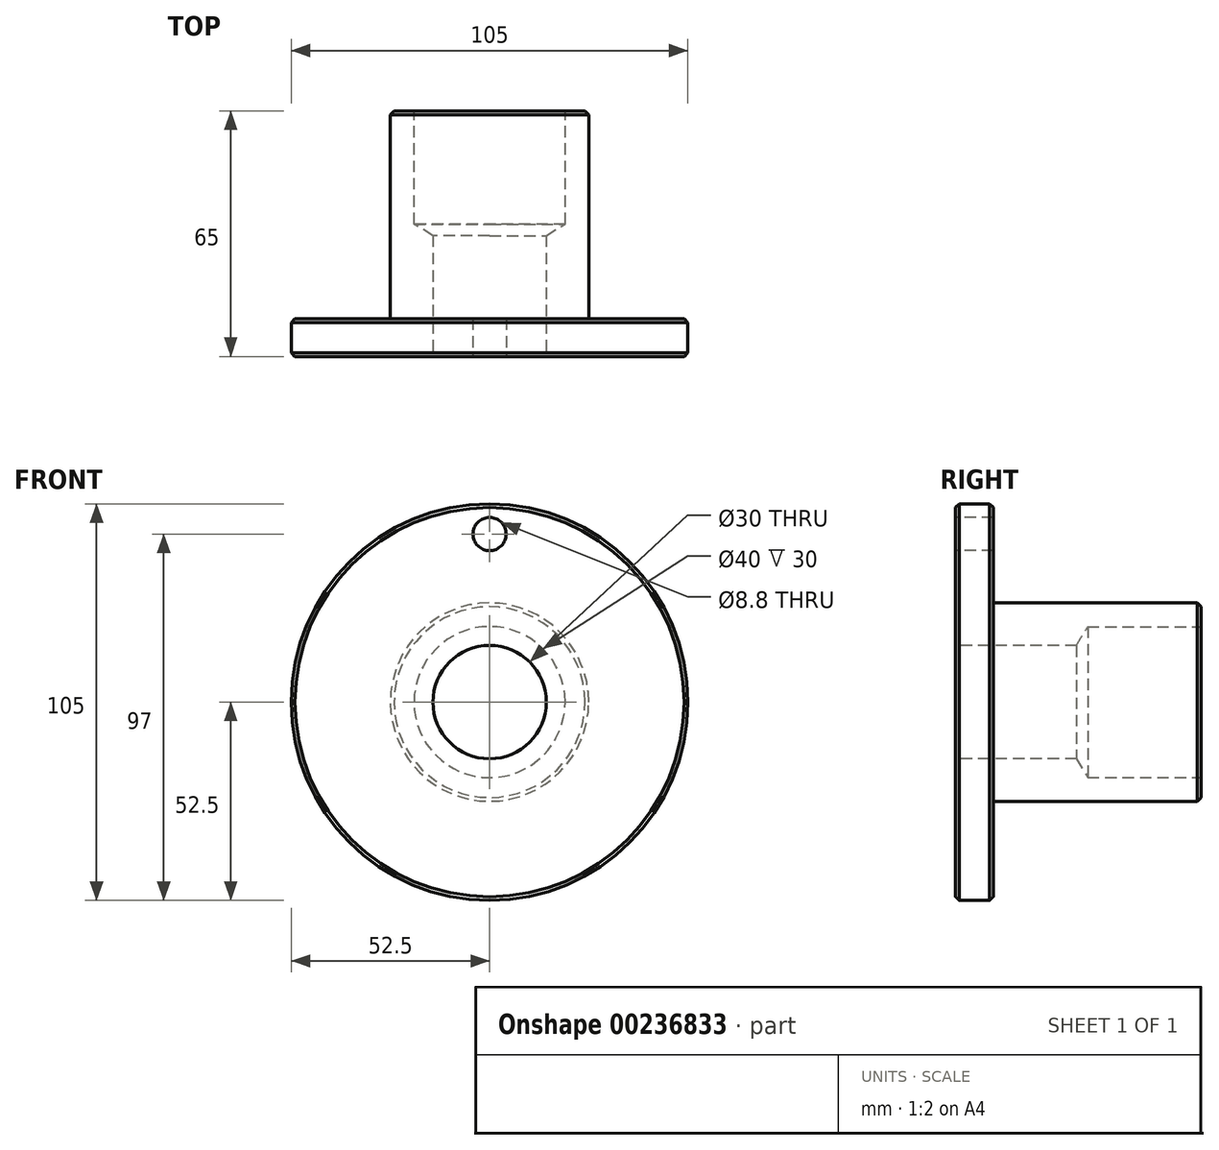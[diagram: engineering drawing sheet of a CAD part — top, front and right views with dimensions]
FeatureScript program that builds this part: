
annotation { "Feature Type Name" : "Feature", "Feature Type Description" : "" }
export const myFeature = defineFeature(function(context is Context, id is Id, definition is map)
    precondition{}
    {
        {
            var Q0;
            Q0=qCreatedBy(makeId("Front.planeOp"),FACE);
            var sketch = newSketch(context, id + "F0", { "sketchPlane" : qUnion([Q0])});
            skCircle(sketch, "E0", {"center": v(0, 0) * mm, "radius": 26.25 * mm});
            skSolve(sketch);
        }
        {
            var Q0;
            Q0=makeQuery(id+"F0.imprint","IMPRINT",FACE,{"disambiguationData":[TD([[makeQuery(id+"F0.imprint","IMPRINT",EDGE,{"derivedFrom":sQuery(id+"F0.wireOp",EDGE,"E0")}),1.0]])]});
            extrude(context, id + "F1", {"entities" : qUnion([Q0]), "depth" : 55 * mm});
        }
        {
            var Q0;
            Q0=makeQuery(id+"F1.opExtrude","CAP_FACE",FACE,{"disambiguationData":[OSD([sQuery(id+"F0.wireOp",EDGE,"E0")])],"isStart":false});
            var sketch = newSketch(context, id + "F2", { "sketchPlane" : qUnion([Q0])});
            skCircle(sketch, "E1", {"center": v(0, 0) * mm, "radius": 52.5 * mm});
            skSolve(sketch);
        }
        {
            var Q0;
            Q0=makeQuery(id+"F2.imprint","IMPRINT",FACE,{"disambiguationData":[TD([[makeQuery(id+"F2.imprint","IMPRINT",EDGE,{"derivedFrom":sQuery(id+"F2.wireOp",EDGE,"E1")}),1.0]])]});
            var Q1;
            Q1=makeQuery(id+"F2.imprint","IMPRINT",FACE,{"disambiguationData":[TD([[makeQuery(id+"F2.imprint","IMPRINT",EDGE,{"derivedFrom":makeQuery(id+"F1.opExtrude","CAP_EDGE",EDGE,{"disambiguationData":[OSD([sQuery(id+"F0.wireOp",EDGE,"E0")])],"isStart":false})}),1.0]])]});
            extrude(context, id + "F3", {"entities" : qUnion([Q0, Q1]), "operationType" : NewBodyOperationType.ADD, "depth" : 10 * mm});
        }
        {
            var Q0;
            Q0=makeQuery(id+"F3.opExtrude","CAP_FACE",FACE,{"disambiguationData":[OSD([sQuery(id+"F2.wireOp",EDGE,"E1")])],"isStart":false});
            var sketch = newSketch(context, id + "F4", { "sketchPlane" : qUnion([Q0])});
            skPoint(sketch, "E2", {"position": v(0, 0) * mm});
            skSolve(sketch);
        }
        {
            var Q0;
            Q0=makeQuery(id+"F1.opExtrude","CAP_FACE",FACE,{"disambiguationData":[OSD([sQuery(id+"F0.wireOp",EDGE,"E0")])],"isStart":true});
            var sketch = newSketch(context, id + "F5", { "sketchPlane" : qUnion([Q0])});
            skPoint(sketch, "E3", {"position": v(0, 0) * mm});
            skSolve(sketch);
        }
        {
            var Q0;
            Q0=sQuery(id+"F4.wireOp",VERTEX,"E2");
            var Q1;
            Q1=makeQuery(id+"F1.opExtrude","SWEPT_BODY",BODY,{"disambiguationData":[OSD([sQuery(id+"F0.wireOp",EDGE,"E0")])]});
            hole(context, id + "F6", {"style" : HoleStyle.SIMPLE, "endStyle" : HoleEndStyle.BLIND, "holeDiameter" : 30 * mm, "holeDepth" : 40 * mm, "locations" : qUnion([Q0]), "scope" : qUnion([Q1])});
        }
        {
            var Q0;
            Q0=sQuery(id+"F5.wireOp",VERTEX,"E3");
            var Q1;
            Q1=makeQuery(id+"F1.opExtrude","SWEPT_BODY",BODY,{"disambiguationData":[OSD([sQuery(id+"F0.wireOp",EDGE,"E0")])]});
            hole(context, id + "F7", {"style" : HoleStyle.SIMPLE, "endStyle" : HoleEndStyle.BLIND, "holeDiameter" : 40 * mm, "holeDepth" : 30 * mm, "locations" : qUnion([Q0]), "scope" : qUnion([Q1])});
        }
        {
            var Q0;
            Q0=makeQuery(id+"F3.opExtrude","CAP_EDGE",EDGE,{"disambiguationData":[OSD([sQuery(id+"F2.wireOp",EDGE,"E1")])],"isStart":true});
            var Q1;
            Q1=makeQuery(id+"F6.hole-0.boolean.opBoolean","COPY",EDGE,{"derivedFrom":makeQuery(id+"F6.hole-0.opRevolve","SWEPT_EDGE",EDGE,{"disambiguationData":[OSD([sQuery(id+"F6.hole-0.sketch.wireOp",EDGE,"core_line_2"),sQuery(id+"F6.hole-0.sketch.wireOp",EDGE,"core_line_3")])]})});
            var Q2;
            Q2=makeQuery(id+"F7.hole-0.boolean.opBoolean","COPY",EDGE,{"derivedFrom":makeQuery(id+"F7.hole-0.opRevolve","SWEPT_EDGE",EDGE,{"disambiguationData":[OSD([sQuery(id+"F7.hole-0.sketch.wireOp",EDGE,"core_line_2"),sQuery(id+"F7.hole-0.sketch.wireOp",EDGE,"core_line_3")])]})});
            var Q3;
            Q3=makeQuery(id+"F7.hole-0.boolean.opBoolean","INTERSECT",EDGE,{"derivedFrom":[makeQuery(id+"F6.hole-0.boolean.opBoolean","COPY",FACE,{"derivedFrom":makeQuery(id+"F6.hole-0.opRevolve","SWEPT_FACE",FACE,{"disambiguationData":[OSD([sQuery(id+"F6.hole-0.sketch.wireOp",EDGE,"core_line_2")])]})}),makeQuery(id+"F7.hole-0.opRevolve","SWEPT_FACE",FACE,{"disambiguationData":[OSD([sQuery(id+"F7.hole-0.sketch.wireOp",EDGE,"core_line_1")])]})]});
            var Q4;
            Q4=makeQuery(id+"F1.opExtrude","CAP_EDGE",EDGE,{"disambiguationData":[OSD([sQuery(id+"F0.wireOp",EDGE,"E0")])],"isStart":true});
            var Q5;
            Q5=makeQuery(id+"F3.opExtrude","CAP_EDGE",EDGE,{"disambiguationData":[OSD([sQuery(id+"F2.wireOp",EDGE,"E1")])],"isStart":false});
            chamfer(context, id + "F8", {"entities" : qUnion([Q0, Q1, Q2, Q3, Q4, Q5]), "width" : 1 * mm, "tangentPropagation" : true});
        }
        {
            var Q0;
            Q0=makeQuery(id+"F3.opExtrude","CAP_FACE",FACE,{"disambiguationData":[OSD([sQuery(id+"F2.wireOp",EDGE,"E1")])],"isStart":false});
            var sketch = newSketch(context, id + "F9", { "sketchPlane" : qUnion([Q0])});
            skPoint(sketch, "E4", {"position": v(0, 44.5) * mm});
            skSolve(sketch);
        }
        {
            var Q0;
            Q0=sQuery(id+"F9.wireOp",VERTEX,"E4");
            var Q1;
            Q1=makeQuery(id+"F1.opExtrude","SWEPT_BODY",BODY,{"disambiguationData":[OSD([sQuery(id+"F0.wireOp",EDGE,"E0")])]});
            hole(context, id + "F10", {"style" : HoleStyle.SIMPLE, "endStyle" : HoleEndStyle.THROUGH, "standardTappedOrClearance" : lookupTablePath({ "standard" : "ISO", "engagement" : "75%", "pitch" : "1.25 mm", "size" : "M10", "type" : "Tapped" }), "standardBlindInLast" : lookupTablePath({ "standard" : "ISO", "engagement" : "75%", "pitch" : "1.25 mm", "size" : "M10", "type" : "Tapped" }), "holeDiameter" : 8.8 * mm, "locations" : qUnion([Q0]), "scope" : qUnion([Q1]), "isTappedThrough" : true, "majorDiameter" : 10 * mm, "showTappedDepth" : true});
        }
    });
